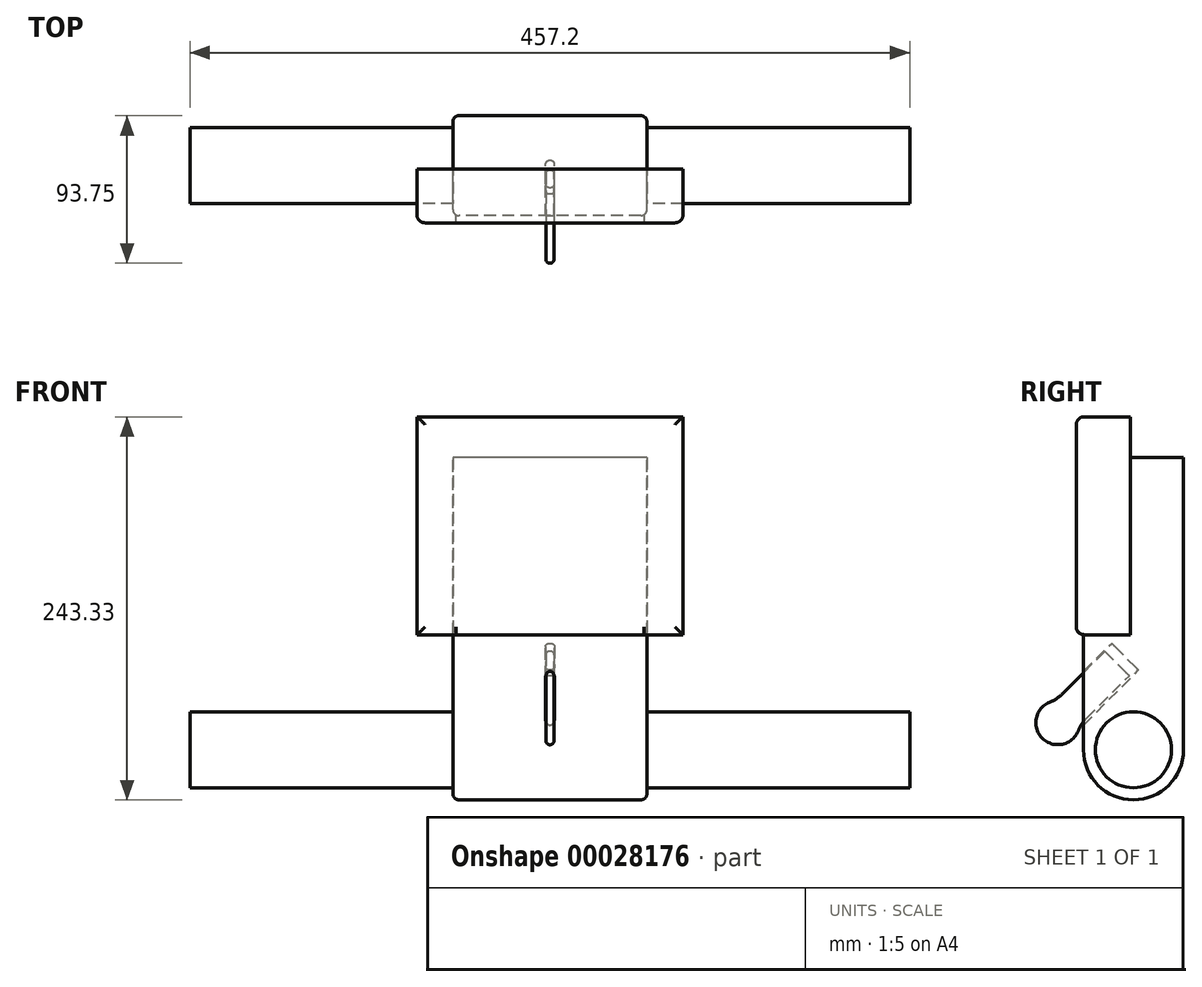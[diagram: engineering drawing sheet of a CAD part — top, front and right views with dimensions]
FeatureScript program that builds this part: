
annotation { "Feature Type Name" : "Feature", "Feature Type Description" : "" }
export const myFeature = defineFeature(function(context is Context, id is Id, definition is map)
    precondition{}
    {
        {
            var Q0;
            Q0=qCreatedBy(makeId("Right.planeOp"),FACE);
            var sketch = newSketch(context, id + "F0", { "sketchPlane" : qUnion([Q0])});
            skArc(sketch, "E0", {"start": v(-31.75, 0) * mm, "mid": v(0, -31.75) * mm, "end": v(31.75, 0) * mm});
            skLineSegment(sketch, "E1", {"start": v(-31.75, 0) * mm, "end": v(-31.75, 73.15) * mm});
            skLineSegment(sketch, "E2", {"start": v(-31.75, 73.15) * mm, "end": v(-2.03, 73.15) * mm});
            skLineSegment(sketch, "E3", {"start": v(-2.03, 73.15) * mm, "end": v(-2.03, 185.67) * mm});
            skLineSegment(sketch, "E4", {"start": v(-2.03, 185.67) * mm, "end": v(31.75, 185.67) * mm});
            skLineSegment(sketch, "E5", {"start": v(31.75, 185.67) * mm, "end": v(31.75, 0) * mm});
            skLineSegment(sketch, "E6", {"start": v(-31.75, 73.15) * mm, "end": v(-36.32, 73.15) * mm, "construction": true});
            skLineSegment(sketch, "E7", {"start": v(-36.32, 73.15) * mm, "end": v(-36.32, 211.58) * mm, "construction": true});
            skLineSegment(sketch, "E8", {"start": v(-36.32, 211.58) * mm, "end": v(-2.03, 211.58) * mm, "construction": true});
            skLineSegment(sketch, "E9", {"start": v(-2.03, 211.58) * mm, "end": v(-2.03, 185.67) * mm, "construction": true});
            skCircle(sketch, "E10", {"center": v(0, 0) * mm, "radius": 24.13 * mm, "construction": true});
            skSolve(sketch);
        }
        {
            var Q0;
            Q0 = qSketchRegion(id + "F0", true);
            extrude(context, id + "F1", {"entities" : qUnion([Q0]), "endBound" : BoundingType.SYMMETRIC, "depth" : 123.19 * mm});
        }
        {
            var Q0;
            Q0=makeQuery(id+"F1.opExtrude","SWEPT_FACE",FACE,{"disambiguationData":[OSD([sQuery(id+"F0.wireOp",EDGE,"E3")])]});
            var sketch = newSketch(context, id + "F2", { "sketchPlane" : qUnion([Q0])});
            skLineSegment(sketch, "E11.bottom", {"start": v(-84.46, 211.58) * mm, "end": v(84.46, 211.58) * mm});
            skLineSegment(sketch, "E11.top", {"start": v(-84.46, 73.15) * mm, "end": v(84.46, 73.15) * mm});
            skLineSegment(sketch, "E11.left", {"start": v(-84.46, 211.58) * mm, "end": v(-84.46, 73.15) * mm});
            skLineSegment(sketch, "E11.right", {"start": v(84.45, 211.58) * mm, "end": v(84.45, 73.15) * mm});
            skPoint(sketch, "E12", {"position": v(0, 73.15) * mm});
            skSolve(sketch);
        }
        {
            var Q0;
            Q0 = qSketchRegion(id + "F2", true);
            extrude(context, id + "F3", {"entities" : qUnion([Q0]), "operationType" : NewBodyOperationType.ADD, "depth" : 34.3 * mm});
        }
        {
            var Q0;
            Q0=qCreatedBy(makeId("Right.planeOp"),FACE);
            var sketch = newSketch(context, id + "F4", { "sketchPlane" : qUnion([Q0])});
            skCircle(sketch, "E13", {"center": v(0, 0) * mm, "radius": 24.13 * mm});
            skSolve(sketch);
        }
        {
            var Q0;
            Q0 = qSketchRegion(id + "F4", true);
            extrude(context, id + "F5", {"entities" : qUnion([Q0]), "operationType" : NewBodyOperationType.ADD, "endBound" : BoundingType.SYMMETRIC, "depth" : 457.2 * mm});
        }
        {
            var Q0;
            Q0=qCreatedBy(makeId("Top.planeOp"),FACE);
            var sketch = newSketch(context, id + "F6", { "sketchPlane" : qUnion([Q0])});
            skLineSegment(sketch, "E14", {"start": v(0, 0) * mm, "end": v(149.31, 0) * mm, "construction": true});
            skSolve(sketch);
        }
        {
            var Q0;
            Q0=sQuery(id+"F6.wireOp",EDGE,"E14");
            cPlane(context, id + "F7", {"entities" : qUnion([Q0]), "cplaneType" : CPlaneType.LINE_ANGLE, "offset" : 152.4 * mm, "angle" : 45 * degree, "width" : 152.4 * mm, "height" : 152.4 * mm});
        }
        {
            var Q0;
            Q0=qCreatedBy(id+"F7.planeOp",FACE);
            var sketch = newSketch(context, id + "F8", { "sketchPlane" : qUnion([Q0])});
            skArc(sketch, "E15", {"start": v(2.86, 54.8) * mm, "mid": v(0, 57.67) * mm, "end": v(-2.86, 54.8) * mm});
            skArc(sketch, "E16", {"start": v(-2.86, 36.4) * mm, "mid": v(0, 33.54) * mm, "end": v(2.86, 36.4) * mm});
            skLineSegment(sketch, "E17", {"start": v(2.86, 54.8) * mm, "end": v(2.86, 36.4) * mm});
            skLineSegment(sketch, "E18", {"start": v(-2.86, 54.8) * mm, "end": v(-2.86, 36.4) * mm});
            skSolve(sketch);
        }
        {
            var Q0;
            Q0 = qSketchRegion(id + "F8", true);
            extrude(context, id + "F9", {"entities" : qUnion([Q0]), "operationType" : NewBodyOperationType.REMOVE, "endBound" : BoundingType.SYMMETRIC, "oppositeDirection" : true, "depth" : 76.2 * mm});
        }
        {
            var Q0;
            Q0=makeQuery(id+"F1.opExtrude","CAP_EDGE",EDGE,{"disambiguationData":[OSD([sQuery(id+"F0.wireOp",EDGE,"E1")])],"isStart":true});
            var Q1;
            Q1=makeQuery(id+"F1.opExtrude","CAP_EDGE",EDGE,{"disambiguationData":[OSD([sQuery(id+"F0.wireOp",EDGE,"E1")])],"isStart":false});
            fillet(context, id + "F10", {"entities" : qUnion([Q0, Q1]), "radius" : 3.8 * mm, "tangentPropagation" : true, "allowEdgeOverflow" : false});
        }
        {
            var Q0;
            Q0=makeQuery(id+"F3.opExtrude","CAP_EDGE",EDGE,{"disambiguationData":[OSD([sQuery(id+"F2.wireOp",EDGE,"E11.right")])],"isStart":false});
            var Q1;
            Q1=makeQuery(id+"F3.opExtrude","CAP_EDGE",EDGE,{"disambiguationData":[OSD([sQuery(id+"F2.wireOp",EDGE,"E11.bottom")])],"isStart":false});
            var Q2;
            Q2=makeQuery(id+"F3.opExtrude","CAP_EDGE",EDGE,{"disambiguationData":[OSD([sQuery(id+"F2.wireOp",EDGE,"E11.left")])],"isStart":false});
            var Q3;
            Q3=makeQuery(id+"F3.opExtrude","CAP_EDGE",EDGE,{"disambiguationData":[OSD([sQuery(id+"F2.wireOp",EDGE,"E11.top")])],"isStart":false});
            fillet(context, id + "F11", {"entities" : qUnion([Q0, Q1, Q2, Q3]), "radius" : 5.08 * mm, "tangentPropagation" : true, "allowEdgeOverflow" : false});
        }
        {
            var Q0;
            Q0=qCreatedBy(makeId("Right.planeOp"),FACE);
            var sketch = newSketch(context, id + "F12", { "sketchPlane" : qUnion([Q0])});
            skLineSegment(sketch, "E19", {"start": v(-34.15, 15.69) * mm, "end": v(-2.72, 47.12) * mm});
            skLineSegment(sketch, "E20", {"start": v(-2.72, 47.12) * mm, "end": v(-18.17, 62.56) * mm});
            skLineSegment(sketch, "E21", {"start": v(-18.17, 62.56) * mm, "end": v(-49.6, 31.13) * mm});
            skArc(sketch, "E22", {"start": v(-49.6, 31.13) * mm, "mid": v(-57.91, 7.37) * mm, "end": v(-34.15, 15.69) * mm});
            skPoint(sketch, "E23", {"position": v(-10.44, 54.84) * mm});
            skLineSegment(sketch, "E24", {"start": v(-49.6, 31.13) * mm, "end": v(-34.15, 15.69) * mm, "construction": true});
            skSolve(sketch);
        }
        {
            var Q0;
            Q0 = qSketchRegion(id + "F12", true);
            extrude(context, id + "F13", {"entities" : qUnion([Q0]), "endBound" : BoundingType.SYMMETRIC, "depth" : 5.08 * mm});
        }
        {
            var Q0;
            Q0=makeQuery(id+"F13.opExtrude","SWEPT_EDGE",EDGE,{"disambiguationData":[OSD([sQuery(id+"F12.wireOp",EDGE,"E21"),sQuery(id+"F12.wireOp",EDGE,"E22")])]});
            var Q1;
            Q1=makeQuery(id+"F13.opExtrude","SWEPT_EDGE",EDGE,{"disambiguationData":[OSD([sQuery(id+"F12.wireOp",EDGE,"E19"),sQuery(id+"F12.wireOp",EDGE,"E22")])]});
            fillet(context, id + "F14", {"entities" : qUnion([Q0, Q1]), "radius" : 24.13 * mm, "tangentPropagation" : true, "allowEdgeOverflow" : false});
        }
        {
            var Q0;
            Q0=makeQuery(id+"F13.opExtrude","CAP_EDGE",EDGE,{"disambiguationData":[OSD([sQuery(id+"F12.wireOp",EDGE,"E19")])],"isStart":true});
            var Q1;
            Q1=makeQuery(id+"F13.opExtrude","CAP_EDGE",EDGE,{"disambiguationData":[OSD([sQuery(id+"F12.wireOp",EDGE,"E19")])],"isStart":false});
            fillet(context, id + "F15", {"entities" : qUnion([Q0, Q1]), "radius" : 2.41 * mm, "tangentPropagation" : true, "allowEdgeOverflow" : false});
        }
    });
